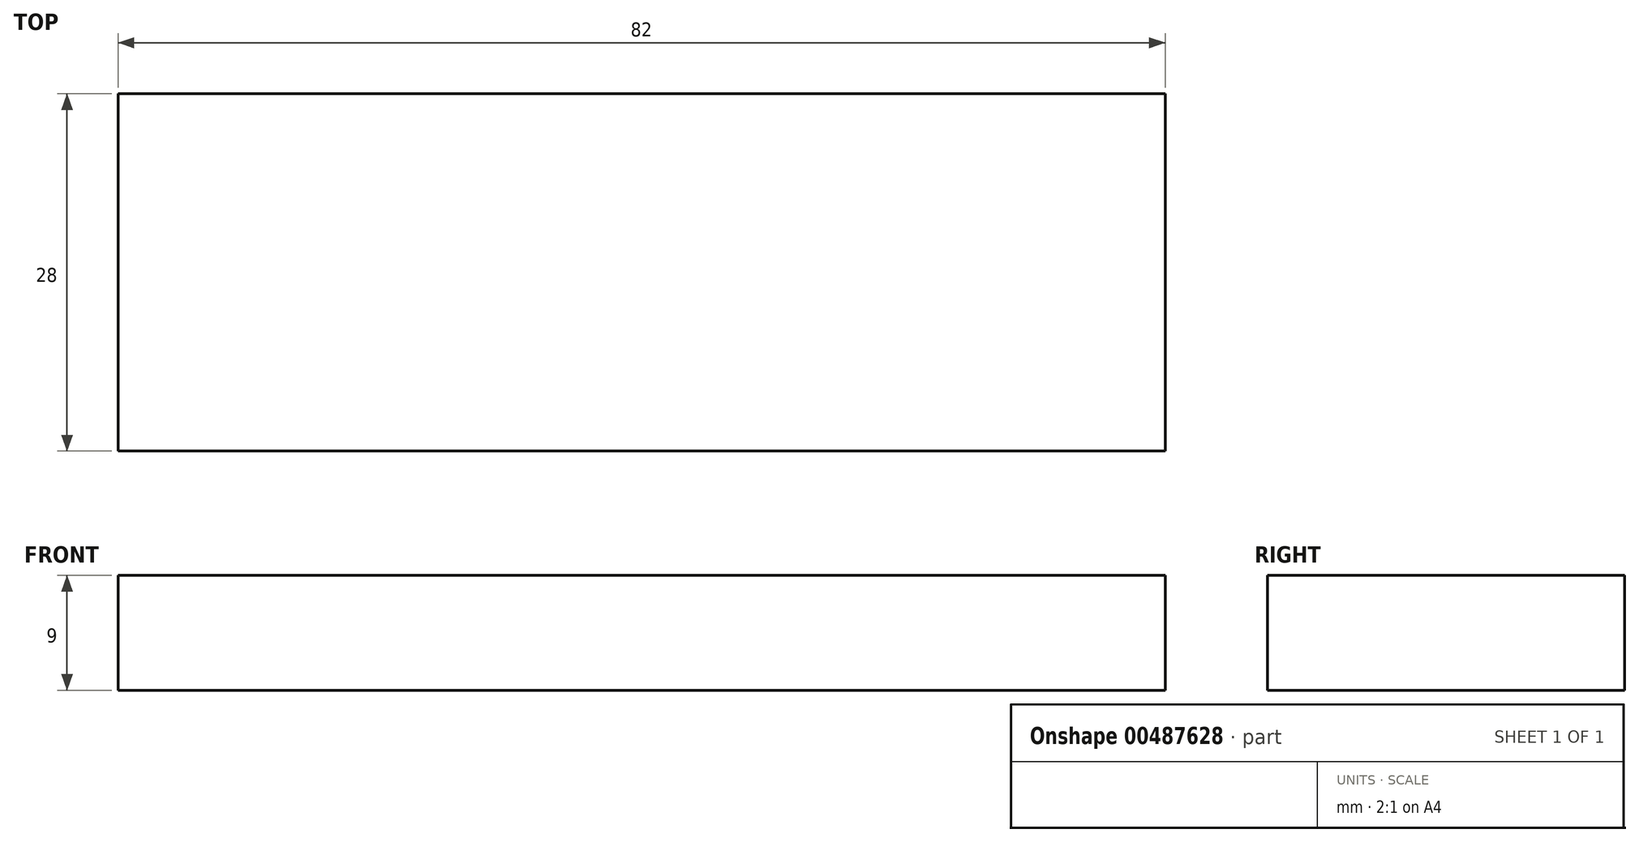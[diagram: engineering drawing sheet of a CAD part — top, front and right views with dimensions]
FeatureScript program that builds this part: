
annotation { "Feature Type Name" : "Feature", "Feature Type Description" : "" }
export const myFeature = defineFeature(function(context is Context, id is Id, definition is map)
    precondition{}
    {
        {
            var Q0;
            Q0=qCreatedBy(makeId("Top.planeOp"),FACE);
            var sketch = newSketch(context, id + "F0", { "sketchPlane" : qUnion([Q0])});
            skLineSegment(sketch, "E0.bottom", {"start": v(41, -14) * mm, "end": v(-41, -14) * mm});
            skLineSegment(sketch, "E0.top", {"start": v(41, 14) * mm, "end": v(-41, 14) * mm});
            skLineSegment(sketch, "E0.left", {"start": v(41, -14) * mm, "end": v(41, 14) * mm});
            skLineSegment(sketch, "E0.right", {"start": v(-41, -14) * mm, "end": v(-41, 14) * mm});
            skPoint(sketch, "E0.middle", {"position": v(0, 0) * mm});
            skSolve(sketch);
        }
        {
            var Q0;
            Q0 = qSketchRegion(id + "F0", true);
            extrude(context, id + "F1", {"entities" : qUnion([Q0]), "depth" : 9 * mm});
        }
    });
